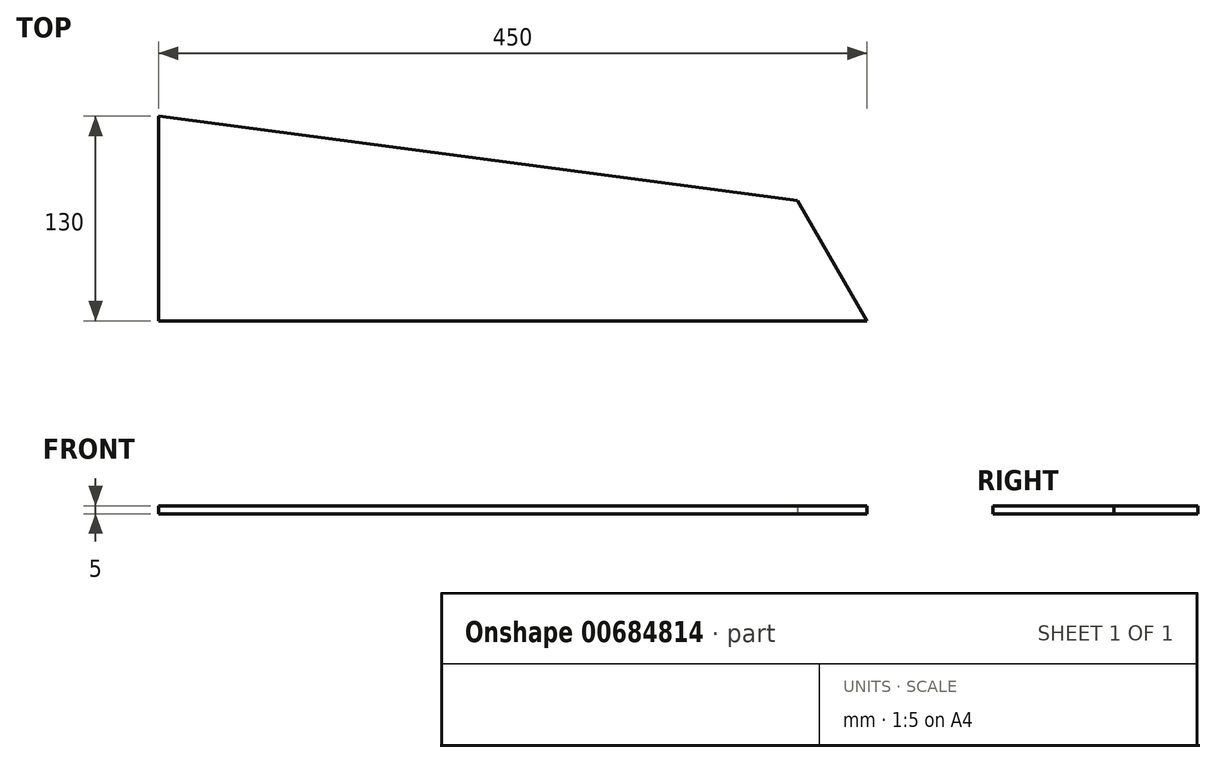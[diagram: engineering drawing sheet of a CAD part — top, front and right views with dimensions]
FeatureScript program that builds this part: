
annotation { "Feature Type Name" : "Feature", "Feature Type Description" : "" }
export const myFeature = defineFeature(function(context is Context, id is Id, definition is map)
    precondition{}
    {
        {
            var Q0;
            Q0=qCreatedBy(makeId("Top.planeOp"),FACE);
            var sketch = newSketch(context, id + "F0", { "sketchPlane" : qUnion([Q0])});
            skLineSegment(sketch, "E0", {"start": v(-186.02, -51.22) * mm, "end": v(263.98, -51.22) * mm});
            skLineSegment(sketch, "E1", {"start": v(-186.02, -51.22) * mm, "end": v(-186.02, 78.78) * mm});
            skLineSegment(sketch, "E2", {"start": v(-186.02, 78.78) * mm, "end": v(219.77, 25.36) * mm});
            skLineSegment(sketch, "E3", {"start": v(219.77, 25.36) * mm, "end": v(263.98, -51.22) * mm});
            skSolve(sketch);
        }
        {
            var Q0;
            Q0=makeQuery(id+"F0.imprint","IMPRINT",FACE,{"disambiguationData":[TD([[makeQuery(id+"F0.imprint","IMPRINT",EDGE,{"derivedFrom":sQuery(id+"F0.wireOp",EDGE,"E0")}),1.0]])]});
            extrude(context, id + "F1", {"entities" : qUnion([Q0]), "depth" : 5 * mm, "offsetDistance" : 25 * mm});
        }
    });
